# Revit family: QF_ELECTROLUXPROFESSIONAL_1L059Y_TD6-14_HP
name_source: partatom
category: Attrezzature speciali
units: mm (PartAtom-declared; Revit-internal decimal feet)

## family parameters
Basato su piano di lavoro = No
Condiviso = No
Punto di calcolo locali = No
Quota connettore circolare = Usa diametro
Sempre verticale = Sì
Taglio con vuoti quando caricato = No
Tipo di parte = Normale

## types (34) — shared parameters
Height Actual = 1771 mm  [stored 5.81037 ft]
Latent Heat Output = 0.0
Length Actual = 790 mm  [stored 2.59186 ft]
Modello = TD6-14
Produttore = Electrolux Professional
Sensible Heat Output = 0.0
URL = www.electroluxprofessional.com
zero-valued in all types: Gas KW, Prospetto di default, Steam Pounds per Hour

## per-type parameters (varying)
| type | Cycle | Depth Actual | Descrizione | Item Number | Phase | Volts | Watts | Weight |
| 9873730067 | 50 Hz | 990 mm  [stored 3.24803 ft] | TUMBLE DRYER TD6-14 14KG GALVA.DRUM HEAT PUMP 400/50/3 COMPASS PRO 6A81 EU SILVER DO.RIGHT.INS. ELS-NETW. PREP.CB MB DIS | 1LSN3Z | 3 | 400 V | 6500 W | 273 |
| 9873730077 | 50 Hz | 990 mm  [stored 3.24803 ft] | TUMBLE DRYER TD6-14 14KG GALVA.DRUM HEAT PUMP 400/50/3 COMPASS PRO 6L80 EU SILVER DO.RIGHT EXT.PM. DISCON. 2.I/O | 1L0EL8 | 3 | 400 V | 6500 W | 273 |
| 9873730204 | 60 Hz | 965 mm  [stored 3.16601 ft] | TUMBLE DRYER TD6-14 14KG SST DRUM HEAT PUMP 200/60/1 COMPASS PRO 6L85 JP SILVER DO.RIGHT.INS. DISCON. | 1L0HAX | 1 | 200 V | 5500 W | 222 |
| 9873730017 | 50 Hz | 990 mm  [stored 3.24803 ft] | TUMBLE DRYER TD6-14 14KG GALVA.DRUM HEAT PUMP 380-415/50/3N COMPASS PRO 6G81 EU SILVER DO.RIGHT.INS. MB DSC STOP DISCON. | 1L0E95 | 3 | 415 V | 6500 W | 273 |
| 9873730113 | 50 Hz | 990 mm  [stored 3.24803 ft] | TUMBLE DRYER TD6-14 14KG GALVA.DRUM HEAT PUMP 400/50/3 COMPASS PRO 6L80 EU SILVER DO.LEFT DISCON. | 1LSNS9 | 3 | 400 V | 6500 W | 273 |
| 9873730180 | 60 Hz | 990 mm  [stored 3.24803 ft] | TUMBLE DRYER TD6-14 14KG SST DRUM HEAT PUMP 480/60/3 COMPASS PRO 6G81 EU SILVER DO.LEFT MB STOP DISCON. | 1L0GYC | 3 | 480 V | 6500 W | 273 |
| 988919413 | 50 Hz | 965 mm  [stored 3.16601 ft] | Spare Part HP255 HP42CC | 1L80GV | 3 | 415 V | 6500 W | 222 |
| 9873730170 | 50 Hz | 990 mm  [stored 3.24803 ft] | TUMBLE DRYER TD6-14 14KG SST DRUM HEAT PUMP 380-415/50/3N COMPASS PRO 6A81 SE SILVER DO.LEFT.INS. MB | 1L0GKV | 3 | 415 V | 6500 W | 273 |
| 9873730110 | 50 Hz | 990 mm  [stored 3.24803 ft] | TUMBLE DRYER TD6-14 14KG SST DRUM HEAT PUMP 400/50/3N COMPASS PRO 6G81 EU SILVER DO.RIGHT MB STOP DISCON. | 1LSNR5 | 3 | 400 V | 6500 W | 273 |
| 9873730202 | 60 Hz | 965 mm  [stored 3.16601 ft] | TUMBLE DRYER TD6-14 14KG SST DRUM HEAT PUMP 200/60/1 COMPASS PRO 6G85 JP SILVER DO.RIGHT.INS. ELS-NETW. MB DISCON. | 1L0HAV | 1 | 200 V | 5500 W | 222 |
| 9873730142 | 50 Hz | 990 mm  [stored 3.24803 ft] | TUMBLE DRYER TD6-14 14KG GALVA.DRUM HEAT PUMP 400/50/3N COMPASS PRO 6A81 EU SILVER DO.RIGHT.INS. ELS-NETW. PREP.CB MB DI | 1LA0A1 | 3 | 400 V | 6500 W | 273 |
| 9873730064 | 50 Hz | 990 mm  [stored 3.24803 ft] | TUMBLE DRYER TD6-14 14KG SST DRUM HEAT PUMP 220/50/1N COMPASS PRO 6G81 EU SILVER DO.LEFT MB STOP DISCON. | 1L80FH | 1 | 220 V | 5500 W | 273 |
| 9873730172 | 50 Hz | 990 mm  [stored 3.24803 ft] | TUMBLE DRYER TD6-14 14KG SST DRUM HEAT PUMP 400/50/3N COMPASS PRO 6L80 EU SILVER DO.RIGHT EXT.PM. DISCON. 2.I/O | 1L99A0 | 3 | 400 V | 6500 W | 273 |
| 9873730132 | 50 Hz | 990 mm  [stored 3.24803 ft] | TUMBLE DRYER TD6-14 14KG GALVA.DRUM HEAT PUMP 220-240/50/1N COMPASS PRO 6L80 EU SILVER DO.RIGHT DISCON. | 1LSNZF | 1 | 240 V | 5500 W | 273 |
| 9873730063 | 60 Hz | 990 mm  [stored 3.24803 ft] | TUMBLE DRYER TD6-14 14KG GALVA.DRUM HEAT PUMP 400/60/3 COMPASS PRO 6G81 EU SILVER DO.RIGHT MB STOP DISCON. | 1L80FG | 3 | 400 V | 6500 W | 273 |
| 9873730147 | 50 Hz | 990 mm  [stored 3.24803 ft] | TUMBLE DRYER TD6-14 14KG GALVA.DRUM HEAT PUMP 400/50/3N COMPASS PRO 6G81 EU SILVER DO.RIGHT MB STOP DISCON. | 1L0GB3 | 3 | 400 V | 6500 W | 273 |
| 9873730167 | 60 Hz | 965 mm  [stored 3.16601 ft] | TUMBLE DRYER TD6-14 14KG GALVA.DRUM HEAT PUMP 220/60/1N COMPASS PRO 6G81 EU SILVER DO.LEFT MB STOP DISCON. | 1L0GJF | 1 | 220 V | 5500 W | 222 |
| 9873730177 | 50 Hz | 990 mm  [stored 3.24803 ft] | TUMBLE DRYER TD6-14 14KG SST DRUM HEAT PUMP 400/50/3N COMPASS PRO 6G81 EU SILVER DO.LEFT.INS. MB STOP DISCON. | 1L0GUV | 3 | 400 V | 6500 W | 273 |
| 9873730208 | 50 Hz | 965 mm  [stored 3.16601 ft] | TUMBLE DRYER TD6-14 14KG GALVA.DRUM HEAT PUMP 380-415/50/3N COMPASS PRO 6G81 EU SILVER DO.LEFT MB STOP DISCON. | 1L82D2 | 3 | 415 V | 6200 W | 222 |
| 9873730203 | 50 Hz | 965 mm  [stored 3.16601 ft] | TUMBLE DRYER TD6-14 14KG SST DRUM HEAT PUMP 200/50/1 COMPASS PRO 6L85 JP SILVER DO.RIGHT.INS. DISCON. | 1L0HAW | 1 | 200 V | 5500 W | 222 |
| 9873730016 | 50 Hz | 990 mm  [stored 3.24803 ft] | TUMBLE DRYER TD6-14 14KG GALVA.DRUM HEAT PUMP 380-415/50/3N COMPASS PRO 6A81 SE SILVER DO.LEFT.INS. MB | 1L0E94 | 3 | 415 V | 6200 W | 273 |
| 9873730141 | 50 Hz | 990 mm  [stored 3.24803 ft] | TUMBLE DRYER TD6-14 14KG GALVA.DRUM HEAT PUMP 400/50/3N COMPASS PRO 6G81 EU SILVER DO.RIGHT MB STOP DISCON. | 1LA0A0 | 3 | 400 V | 6500 W | 273 |
| 9873730206 | 50 Hz | 965 mm  [stored 3.16601 ft] | TUMBLE DRYER TD6-14 14KG GALVA.DRUM HEAT PUMP 380-415/50/3N COMPASS PRO 6G81 EU SILVER DO.RIGHT.INS. MB STOP DISCON. | 1LM0BD | 3 | 415 V | 6200 W | 222 |
| 9873730015 | 50 Hz | 990 mm  [stored 3.24803 ft] | TUMBLE DRYER TD6-14 14KG GALVA.DRUM HEAT PUMP 220-240/50/1N COMPASS PRO 6G81 EU SILVER DO.RIGHT.INS. MB STOP DISCON. | 1L0E93 | 1 | 240 V | 5500 W | 273 |
| 9873730201 | 50 Hz | 965 mm  [stored 3.16601 ft] | TUMBLE DRYER TD6-14 14KG SST DRUM HEAT PUMP 200/50/1 COMPASS PRO 6G85 JP SILVER DO.RIGHT.INS. ELS-NETW. MB DISCON. | 1L0HAU | 1 | 200 V | 5500 W | 222 |
| 9873730186 | 50 Hz | 965 mm  [stored 3.16601 ft] | TUMBLE DRYER TD6-14 14KG SST DRUM HEAT PUMP 400/50/3N COMPASS PRO 6G81 EU SILVER DO.RIGHT.INS. MB DSC STOP DISCON. | 1LSPNF | 3 | 400 V | 6500 W | 222 |
| 9873730221 | 50 Hz | 965 mm  [stored 3.16601 ft] | TUMBLE DRYER TD6-14 14KG SST DRUM HEAT PUMP 230/50/1N COMPASS PRO 6L80 EU SILVER DO.RIGHT EXT.PM. DISCON. 2.I/O | 1LT6KW | 1 | 230 V | 5500 W | 222 |
| 9873730048 | 50 Hz | 990 mm  [stored 3.24803 ft] | TUMBLE DRYER TD6-14 14KG GALVA.DRUM HEAT PUMP 220-240/50/1N COMPASS PRO 6G81 EU SILVER DO.RIGHT MB STOP DISCON. | 1L0EH3 | 1 | 240 V | 5500 W | 273 |
| 9873730058 | 50 Hz | 990 mm  [stored 3.24803 ft] | TUMBLE DRYER TD6-14 14KG GALVA.DRUM HEAT PUMP 220-240/50/1N COMPASS PRO 6A81 EU SILVER DO.RIGHT ELS-NETW. PREP.CB MB DIS | 1L80E2 | 1 | 240 V | 5500 W | 273 |
| 9873730068 | 50 Hz | 990 mm  [stored 3.24803 ft] | TUMBLE DRYER TD6-14 14KG GALVA.DRUM HEAT PUMP 400/50/3 COMPASS PRO 6G81 EU SILVER DO.RIGHT MB STOP DISCON. | 1LSN40 | 3 | 400 V | 6500 W | 273 |
| 9873730078 | 50 Hz | 990 mm  [stored 3.24803 ft] | TUMBLE DRYER TD6-14 14KG GALVA.DRUM HEAT PUMP 380-415/50/3N COMPASS PRO 6L80 EU SILVER DO.LEFT EXT.PM. DISCON. 2.I/O | 1L80GX | 3 | 415 V | 6500 W | 273 |
| 9873730219 | 50 Hz | 965 mm  [stored 3.16601 ft] | TUMBLE DRYER TD6-14 14KG GALVA.DRUM HEAT PUMP 380-415/50/3N COMPASS PRO 6G81 EU SILVER DO.RIGHT.INS. MB STOP DISCON. | 1L0HJG | 3 | 415 V | 6200 W | 222 |
| 9873730166 | 50 Hz | 990 mm  [stored 3.24803 ft] | TUMBLE DRYER TD6-14 14KG SST DRUM HEAT PUMP 230/50/1N COMPASS PRO 6G81 EU SILVER DO.LEFT.INS. MB STOP DISCON. | 1LSPD0 | 1 | 230 V | 5500 W | 273 |
| 9873730143 | 60 Hz | 990 mm  [stored 3.24803 ft] | TUMBLE DRYER TD6-14 14KG GALVA.DRUM HEAT PUMP 440/60/3 COMPASS PRO 6G81 EU SILVER DO.LEFT MB STOP DISCON. | 1LA0AB | 3 | 440 V | 6500 W | 273 |

note: [stored X ft] marks values corroborated as IEEE doubles in the binary element streams (Revit-internal decimal feet)

## geometry (parser evidence)
native form markers: Blend x8
no freeform markers — native parametric forms only
